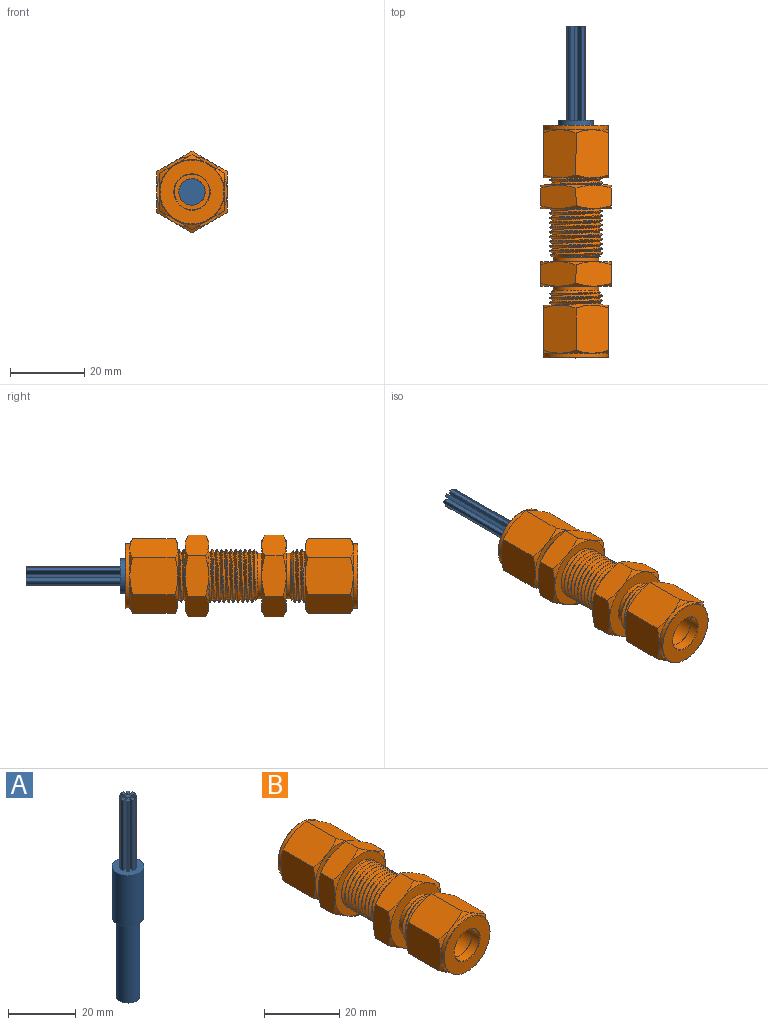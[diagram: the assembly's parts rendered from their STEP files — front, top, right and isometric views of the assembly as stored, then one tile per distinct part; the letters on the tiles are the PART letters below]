
ASSEMBLY  parts=2 mates=1
PART A: 38 faces, bbox 9.4x9.4x72.3 mm
  f0: plane 9.42x9.42mm, normal (0,0,1), area 57.7mm2, adj f3,f5,f6,f7,f8,f9,f10,f11
  f1: cylinder r=3.52mm len=28.65mm, axis (0,0,-1), area 633.3mm2, adj f2,f4
  f2: plane 7.04x7.04mm, normal (0,0,-1), area 38.9mm2, adj f1
  f3: cylinder r=4.71mm len=18.29mm, axis (0,0,-1), area 541.4mm2, adj f0,f4
  f4: plane 9.42x9.42mm, normal (0,0,-1), area 30.9mm2, adj f1,f3
  f5: plane 25.4x1.62mm, normal (-0.2,0.98,0), area 41.9mm2, adj f0,f6,f36,f37
  f6: cylinder r=0.95mm len=25.4mm, axis (0,0,-1), area 9.5mm2, adj f0,f5,f7,f37
  f7: plane 25.4x1.37mm, normal (0.56,-0.83,0), area 41.9mm2, adj f0,f6,f8,f37
  f8: cylinder r=2.6mm len=25.4mm, axis (0,0,-1), area 26mm2, adj f0,f7,f9,f37
  f9: plane 25.4x1.37mm, normal (-0.83,0.56,0), area 41.9mm2, adj f0,f8,f10,f37
  f10: cylinder r=0.95mm len=25.4mm, axis (0,0,-1), area 9.5mm2, adj f0,f9,f11,f37
  f11: plane 25.4x1.62mm, normal (0.98,-0.2,0), area 41.9mm2, adj f0,f10,f12,f37
  f12: cylinder r=2.6mm len=25.4mm, axis (0,0,-1), area 26mm2, adj f0,f11,f13,f37
  f13: plane 25.4x1.62mm, normal (-0.98,-0.2,0), area 41.9mm2, adj f0,f12,f14,f37
  f14: cylinder r=0.95mm len=25.4mm, axis (0,0,-1), area 9.5mm2, adj f0,f13,f15,f37
  f15: plane 25.4x1.37mm, normal (0.83,0.56,0), area 41.9mm2, adj f0,f14,f16,f37
  f16: cylinder r=2.6mm len=25.4mm, axis (0,0,-1), area 26mm2, adj f0,f15,f17,f37
  f17: plane 25.4x1.37mm, normal (-0.56,-0.83,0), area 41.9mm2, adj f0,f16,f18,f37
  f18: cylinder r=0.95mm len=25.4mm, axis (0,0,-1), area 9.5mm2, adj f0,f17,f19,f37
  f19: plane 25.4x1.62mm, normal (0.2,0.98,0), area 41.9mm2, adj f0,f18,f20,f37
  f20: cylinder r=2.6mm len=25.4mm, axis (0,0,-1), area 26mm2, adj f0,f19,f21,f37
  f21: plane 25.4x1.62mm, normal (0.2,-0.98,0), area 41.9mm2, adj f0,f20,f22,f37
  f22: cylinder r=0.95mm len=25.4mm, axis (0,0,-1), area 9.5mm2, adj f0,f21,f23,f37
  f23: plane 25.4x1.37mm, normal (-0.56,0.83,0), area 41.9mm2, adj f0,f22,f24,f37
  f24: cylinder r=2.6mm len=25.4mm, axis (0,0,-1), area 26mm2, adj f0,f23,f25,f37
  f25: plane 25.4x1.37mm, normal (0.83,-0.56,0), area 41.9mm2, adj f0,f24,f26,f37
  f26: cylinder r=0.95mm len=25.4mm, axis (0,0,-1), area 9.5mm2, adj f0,f25,f27,f37
  f27: plane 25.4x1.62mm, normal (-0.98,0.2,0), area 41.9mm2, adj f0,f26,f28,f37
  f28: cylinder r=2.6mm len=25.4mm, axis (0,0,-1), area 26mm2, adj f0,f27,f29,f37
  f29: plane 25.4x1.62mm, normal (0.98,0.2,0), area 41.9mm2, adj f0,f28,f30,f37
  f30: cylinder r=0.95mm len=25.4mm, axis (0,0,-1), area 9.5mm2, adj f0,f29,f31,f37
  f31: plane 25.4x1.37mm, normal (-0.83,-0.56,0), area 41.9mm2, adj f0,f30,f32,f37
  f32: cylinder r=2.6mm len=25.4mm, axis (0,0,-1), area 26mm2, adj f0,f31,f33,f37
  f33: plane 25.4x1.37mm, normal (0.56,0.83,0), area 41.9mm2, adj f0,f32,f34,f37
  f34: cylinder r=0.95mm len=25.4mm, axis (0,0,-1), area 9.5mm2, adj f0,f33,f35,f37
  f35: plane 25.4x1.62mm, normal (-0.2,-0.98,0), area 41.9mm2, adj f0,f34,f36,f37
  f36: cylinder r=2.6mm len=25.4mm, axis (0,0,-1), area 26mm2, adj f0,f5,f35,f37
  f37: plane 5.21x5.21mm, normal (0,0,1), area 12.1mm2, adj f5,f6,f7,f8,f9,f10,f11,f12
PART B: 148 faces, bbox 22.9x63.6x22.9 mm
  f0: plane 19.05x19.05mm, normal (0,1,0), area 124.7mm2, adj f2,f9,f10,f11,f12,f13,f14,f21
  f1: plane 19.05x19.05mm, normal (0,-1,0), area 124.7mm2, adj f2,f3,f4,f5,f6,f7,f8,f55
  f2: cylinder r=7.14mm len=14.29mm, axis (0,-1,0), area 249.4mm2, adj f0,f1,f72,f74
  f3: cone r=9.53mm half-angle=60deg, axis (0,1,0), area 8.9mm2, adj f1,f18,f19
  f4: cone r=9.53mm half-angle=60deg, axis (0,1,0), area 8.9mm2, adj f1,f17,f18
  f5: cone r=9.53mm half-angle=60deg, axis (0,1,0), area 8.9mm2, adj f1,f16,f17
  f6: cone r=9.53mm half-angle=60deg, axis (0,1,0), area 8.9mm2, adj f1,f15,f16
  f7: cone r=9.53mm half-angle=60deg, axis (0,1,0), area 8.9mm2, adj f1,f15,f20
  f8: cone r=9.53mm half-angle=60deg, axis (0,1,0), area 8.9mm2, adj f1,f19,f20
  f9: cone r=11mm half-angle=60deg, axis (0,-1,0), area 8.9mm2, adj f0,f18,f19
  f10: cone r=11mm half-angle=60deg, axis (0,-1,0), area 8.9mm2, adj f0,f17,f18
  f11: cone r=11mm half-angle=60deg, axis (0,-1,0), area 8.9mm2, adj f0,f16,f17
  f12: cone r=11mm half-angle=60deg, axis (0,-1,0), area 8.9mm2, adj f0,f15,f16
  f13: cone r=11mm half-angle=60deg, axis (0,-1,0), area 8.9mm2, adj f0,f15,f20
  f14: cone r=11mm half-angle=60deg, axis (0,-1,0), area 8.9mm2, adj f0,f19,f20
  f15: plane 10.43x7.26mm, normal (-0.5,0,0.87), area 63.4mm2, adj f6,f7,f12,f13,f16,f20
  f16: plane 11.91x7.26mm, normal (-1,0,0), area 63.4mm2, adj f5,f6,f11,f12,f15,f17
  f17: plane 10.43x7.26mm, normal (-0.5,0,-0.87), area 63.4mm2, adj f4,f5,f10,f11,f16,f18
  f18: plane 10.43x7.26mm, normal (0.5,0,-0.87), area 63.4mm2, adj f3,f4,f9,f10,f17,f19
  f19: plane 11.91x7.26mm, normal (1,0,0), area 63.4mm2, adj f3,f8,f9,f14,f18,f20
  f20: plane 10.43x7.26mm, normal (0.5,0,0.87), area 63.4mm2, adj f7,f8,f13,f14,f15,f19
  f21: cylinder r=7.14mm len=14.29mm, axis (0,1,0), area 10.7mm2, adj f0,f22,f72,f74
  f22: plane 17.46x17.46mm, normal (0,-1,0), area 79.2mm2, adj f21,f24,f25,f26,f27,f28,f29,f44
  f23: plane 17.21x17.21mm, normal (0,1,0), area 157.5mm2, adj f53,f54
  f24: cone r=10.08mm half-angle=60deg, axis (0,1,0), area 7.5mm2, adj f22,f31,f32
  f25: cone r=10.08mm half-angle=60deg, axis (0,1,0), area 7.5mm2, adj f22,f32,f33
  f26: cone r=10.08mm half-angle=60deg, axis (0,1,0), area 7.5mm2, adj f22,f33,f34
  f27: cone r=10.08mm half-angle=60deg, axis (0,1,0), area 7.5mm2, adj f22,f34,f35
  f28: cone r=10.08mm half-angle=60deg, axis (0,1,0), area 7.5mm2, adj f22,f30,f35
  f29: cone r=10.08mm half-angle=60deg, axis (0,1,0), area 7.5mm2, adj f22,f30,f31
  f30: plane 13.8x9.56mm, normal (0.5,0,-0.87), area 125.2mm2, adj f28,f29,f31,f35,f37,f42
  f31: plane 13.79x10.92mm, normal (1,0,0), area 125.2mm2, adj f24,f29,f30,f32,f41,f42
  f32: plane 13.8x9.56mm, normal (0.5,0,0.87), area 125.2mm2, adj f24,f25,f31,f33,f40,f41
  f33: plane 13.8x9.56mm, normal (-0.5,0,0.87), area 125.2mm2, adj f25,f26,f32,f34,f39,f40
  f34: plane 13.79x10.92mm, normal (-1,0,0), area 125.2mm2, adj f26,f27,f33,f35,f38,f39
  f35: plane 13.8x9.56mm, normal (-0.5,0,-0.87), area 125.2mm2, adj f27,f28,f30,f34,f37,f38
  f36: cylinder r=8.73mm len=17.46mm, axis (0,1,0), area 62.7mm2, adj f37,f38,f39,f40,f41,f42,f54
  f37: cone r=8.73mm half-angle=60deg, axis (0,-1,0), area 7.5mm2, adj f30,f35,f36
  f38: cone r=8.73mm half-angle=60deg, axis (0,-1,0), area 7.5mm2, adj f34,f35,f36
  f39: cone r=8.73mm half-angle=60deg, axis (0,-1,0), area 7.5mm2, adj f33,f34,f36
  f40: cone r=8.73mm half-angle=60deg, axis (0,-1,0), area 7.5mm2, adj f32,f33,f36
  f41: cone r=8.73mm half-angle=60deg, axis (0,-1,0), area 7.5mm2, adj f31,f32,f36
  f42: cone r=8.73mm half-angle=60deg, axis (0,-1,0), area 7.5mm2, adj f30,f31,f36
  f43: cylinder r=4.76mm len=9.53mm, axis (0,1,0), area 77.5mm2, adj f52,f53
  f44: cylinder r=7.14mm len=14.29mm, axis (0,1,0), area 14mm2, adj f22,f45,f72
  f45: cylinder r=7.14mm len=14.29mm, axis (0,1,0), area 49mm2, adj f22,f44,f46,f72,f74
  f46: cylinder r=7.14mm len=14.29mm, axis (0,1,0), area 49.9mm2, adj f45,f47,f72,f74
  f47: cylinder r=7.14mm len=14.29mm, axis (0,1,0), area 49.9mm2, adj f46,f48,f72,f74
  f48: cylinder r=7.14mm len=14.29mm, axis (0,1,0), area 187.6mm2, adj f47,f49,f72,f74,f109
  f49: plane 14.29x14.29mm, normal (0,-1,0), area 27.2mm2, adj f48,f50
  f50: cylinder r=6.51mm len=13.02mm, axis (0,1,0), area 116.3mm2, adj f49,f51
  f51: plane 13.02x13.02mm, normal (0,-1,0), area 11.4mm2, adj f50,f57
  f52: cone r=4.89mm half-angle=45deg, axis (0,-1,0), area 5.4mm2, adj f43,f56
  f53: cone r=4.76mm half-angle=45deg, axis (0,1,0), area 5.4mm2, adj f23,f43
  f54: cone r=8.6mm half-angle=45deg, axis (0,-1,0), area 9.8mm2, adj f23,f36
  f55: cylinder r=7.14mm len=14.29mm, axis (0,1,0), area 68.4mm2, adj f1,f72,f74,f111
  f56: plane 9.78x9.78mm, normal (0,1,0), area 3.9mm2, adj f52,f60
  f57: cylinder r=6.22mm len=12.45mm, axis (0,1,0), area 44.7mm2, adj f51,f58
  f58: plane 12.45x12.45mm, normal (0,-1,0), area 28.8mm2, adj f57,f59
  f59: cylinder r=5.44mm len=10.87mm, axis (0,1,0), area 26.5mm2, adj f58,f62
  f60: cylinder r=4.76mm len=9.53mm, axis (0,1,0), area 203.3mm2, adj f56,f63
  f61: cone r=5.08mm half-angle=13.9deg, axis (0,1,0), area 102.8mm2, adj f62,f75
  f62: plane 12.57x12.57mm, normal (0,1,0), area 31.3mm2, adj f59,f61
  f63: plane 10.16x10.16mm, normal (0,-1,0), area 9.8mm2, adj f60,f64
  f64: cone r=5.63mm half-angle=13.9deg, axis (0,1,0), area 40.9mm2, adj f63,f106
  f65: cylinder r=6.22mm len=12.45mm, axis (0,-1,0), area 44.7mm2, adj f66,f142
  f66: plane 12.45x12.45mm, normal (0,1,0), area 28.8mm2, adj f65,f67
  f67: cylinder r=5.44mm len=10.87mm, axis (0,-1,0), area 26.5mm2, adj f66,f69
  f68: cone r=5.08mm half-angle=13.9deg, axis (0,-1,0), area 102.8mm2, adj f69,f76
  f69: plane 12.57x12.57mm, normal (0,-1,0), area 31.3mm2, adj f67,f68
  f70: plane 10.16x10.16mm, normal (0,1,0), area 9.8mm2, adj f71,f146
  f71: cone r=4.76mm half-angle=13.9deg, axis (0,-1,0), area 40.9mm2, adj f70,f105
  f72: bspline ~30.3x14.27mm, area 869.4mm2, adj f2,f21,f44,f45,f46,f47,f48,f55
  f73: cylinder r=6.32mm len=27.96mm, axis (0,1,0), area 401.8mm2, adj f72,f74,f109,f110
  f74: bspline ~28.61x14.43mm, area 869.8mm2, adj f2,f21,f45,f46,f47,f48,f55,f73
  f75: plane 12.36x12.36mm, normal (0,1,0), area 20.6mm2, adj f61,f109
  f76: plane 12.36x12.36mm, normal (0,-1,0), area 20.6mm2, adj f68,f80
  f77: plane 19.05x19.05mm, normal (0,-1,0), area 165mm2, adj f79,f85,f86,f87,f88,f89,f90
  f78: cone r=7.28mm half-angle=45deg, axis (0,-1,0), area 31.9mm2, adj f79,f81,f82,f83,f84
  f79: cylinder r=6.18mm len=12.36mm, axis (0,-1,0), area 42.7mm2, adj f77,f78
  f80: cone r=6.18mm half-angle=45deg, axis (0,1,0), area 31.9mm2, adj f76,f81,f82,f83,f113
  f81: bspline ~14.43x14.43mm, area 306mm2, adj f78,f80,f82,f84,f113,f114,f115,f116
  f82: cylinder r=6.32mm len=12.64mm, axis (0,1,0), area 76.4mm2, adj f78,f80,f81,f83
  f83: bspline ~16.4x16.37mm, area 438.8mm2, adj f78,f80,f82,f84,f113,f115,f116,f117
  f84: cylinder r=7.14mm len=14.29mm, axis (0,1,0), area 16.9mm2, adj f78,f81,f83,f118
  f85: cone r=9.53mm half-angle=60deg, axis (0,1,0), area 8.9mm2, adj f77,f91,f92
  f86: cone r=9.53mm half-angle=60deg, axis (0,1,0), area 8.9mm2, adj f77,f92,f93
  f87: cone r=9.53mm half-angle=60deg, axis (0,1,0), area 8.9mm2, adj f77,f93,f94
  f88: cone r=9.53mm half-angle=60deg, axis (0,1,0), area 8.9mm2, adj f77,f94,f95
  f89: cone r=9.53mm half-angle=60deg, axis (0,1,0), area 8.9mm2, adj f77,f95,f96
  f90: cone r=9.53mm half-angle=60deg, axis (0,1,0), area 8.9mm2, adj f77,f91,f96
  f91: plane 11.91x7.52mm, normal (1,0,0), area 66.2mm2, adj f85,f90,f92,f96,f97,f102
  f92: plane 10.43x7.51mm, normal (0.5,0,-0.87), area 66.2mm2, adj f85,f86,f91,f93,f97,f98
  f93: plane 10.43x7.51mm, normal (-0.5,0,-0.87), area 66.2mm2, adj f86,f87,f92,f94,f98,f99
  f94: plane 11.91x7.52mm, normal (-1,0,0), area 66.2mm2, adj f87,f88,f93,f95,f99,f100
  f95: plane 10.43x7.51mm, normal (-0.5,0,0.87), area 66.2mm2, adj f88,f89,f94,f96,f100,f101
  f96: plane 10.43x7.51mm, normal (0.5,0,0.87), area 66.2mm2, adj f89,f90,f91,f95,f101,f102
  f97: cone r=11mm half-angle=60deg, axis (0,-1,0), area 8.9mm2, adj f91,f92,f103
  f98: cone r=11mm half-angle=60deg, axis (0,-1,0), area 8.9mm2, adj f92,f93,f103
  f99: cone r=11mm half-angle=60deg, axis (0,-1,0), area 8.9mm2, adj f93,f94,f103
  f100: cone r=11mm half-angle=60deg, axis (0,-1,0), area 8.9mm2, adj f94,f95,f103
  f101: cone r=11mm half-angle=60deg, axis (0,-1,0), area 8.9mm2, adj f95,f96,f103
  f102: cone r=11mm half-angle=60deg, axis (0,-1,0), area 8.9mm2, adj f91,f96,f103
  f103: plane 19.05x19.05mm, normal (0,1,0), area 165mm2, adj f97,f98,f99,f100,f101,f102,f112
  f104: plane 9.53x9.53mm, normal (0,-1,0), area 31.2mm2, adj f105,f108
  f105: cylinder r=4.76mm len=9.53mm, axis (0,-1,0), area 182.4mm2, adj f71,f104
  f106: cylinder r=4.76mm len=9.53mm, axis (0,-1,0), area 182.4mm2, adj f64,f107
  f107: plane 9.53x9.53mm, normal (0,1,0), area 31.2mm2, adj f106,f108
  f108: cylinder r=3.57mm len=28.64mm, axis (0,-1,0), area 642.2mm2, adj f104,f107
  f109: cone r=7.28mm half-angle=45deg, axis (0,-1,0), area 31.9mm2, adj f48,f72,f73,f74,f75
  f110: cone r=6.18mm half-angle=45deg, axis (0,1,0), area 29.9mm2, adj f72,f73,f74,f111,f112
  f111: cone r=6.18mm half-angle=45deg, axis (0,1,0), area 2.1mm2, adj f55,f72,f74,f110
  f112: cylinder r=6.18mm len=12.36mm, axis (0,-1,0), area 42.7mm2, adj f103,f110
  f113: cylinder r=7.14mm len=14.29mm, axis (0,-1,0), area 186.4mm2, adj f80,f81,f83,f117,f140
  f114: cylinder r=7.14mm len=14.29mm, axis (0,-1,0), area 15mm2, adj f81,f115,f118
  f115: cylinder r=7.14mm len=14.29mm, axis (0,-1,0), area 49.3mm2, adj f81,f83,f114,f116,f118
  f116: cylinder r=7.14mm len=14.29mm, axis (0,-1,0), area 49.9mm2, adj f81,f83,f115,f117
  f117: cylinder r=7.14mm len=14.29mm, axis (0,-1,0), area 49.9mm2, adj f81,f83,f113,f116
  f118: plane 17.46x17.46mm, normal (0,1,0), area 79.2mm2, adj f84,f114,f115,f120,f121,f122,f123,f124
  f119: plane 17.21x17.21mm, normal (0,-1,0), area 157.5mm2, adj f144,f145
  f120: cone r=10.08mm half-angle=60deg, axis (0,-1,0), area 7.5mm2, adj f118,f127,f128
  f121: cone r=10.08mm half-angle=60deg, axis (0,-1,0), area 7.5mm2, adj f118,f128,f129
  f122: cone r=10.08mm half-angle=60deg, axis (0,-1,0), area 7.5mm2, adj f118,f129,f130
  f123: cone r=10.08mm half-angle=60deg, axis (0,-1,0), area 7.5mm2, adj f118,f130,f131
  f124: cone r=10.08mm half-angle=60deg, axis (0,-1,0), area 7.5mm2, adj f118,f126,f131
  f125: cone r=10.08mm half-angle=60deg, axis (0,-1,0), area 7.5mm2, adj f118,f126,f127
  f126: plane 13.8x9.56mm, normal (0.5,0,0.87), area 125.2mm2, adj f124,f125,f127,f131,f133,f138
  f127: plane 13.79x10.92mm, normal (1,0,0), area 125.2mm2, adj f120,f125,f126,f128,f137,f138
  f128: plane 13.8x9.56mm, normal (0.5,0,-0.87), area 125.2mm2, adj f120,f121,f127,f129,f136,f137
  f129: plane 13.8x9.56mm, normal (-0.5,0,-0.87), area 125.2mm2, adj f121,f122,f128,f130,f135,f136
  f130: plane 13.79x10.92mm, normal (-1,0,0), area 125.2mm2, adj f122,f123,f129,f131,f134,f135
  f131: plane 13.8x9.56mm, normal (-0.5,0,0.87), area 125.2mm2, adj f123,f124,f126,f130,f133,f134
  f132: cylinder r=8.73mm len=17.46mm, axis (0,-1,0), area 62.7mm2, adj f133,f134,f135,f136,f137,f138,f145
  f133: cone r=8.73mm half-angle=60deg, axis (0,1,0), area 7.5mm2, adj f126,f131,f132
  f134: cone r=8.73mm half-angle=60deg, axis (0,1,0), area 7.5mm2, adj f130,f131,f132
  f135: cone r=8.73mm half-angle=60deg, axis (0,1,0), area 7.5mm2, adj f129,f130,f132
  f136: cone r=8.73mm half-angle=60deg, axis (0,1,0), area 7.5mm2, adj f128,f129,f132
  f137: cone r=8.73mm half-angle=60deg, axis (0,1,0), area 7.5mm2, adj f127,f128,f132
  f138: cone r=8.73mm half-angle=60deg, axis (0,1,0), area 7.5mm2, adj f126,f127,f132
  f139: cylinder r=4.76mm len=9.53mm, axis (0,-1,0), area 77.5mm2, adj f143,f144
  f140: plane 14.29x14.29mm, normal (0,1,0), area 27.2mm2, adj f113,f141
  f141: cylinder r=6.51mm len=13.02mm, axis (0,-1,0), area 116.3mm2, adj f140,f142
  f142: plane 13.02x13.02mm, normal (0,1,0), area 11.4mm2, adj f65,f141
  f143: cone r=4.89mm half-angle=45deg, axis (0,1,0), area 5.4mm2, adj f139,f147
  f144: cone r=4.76mm half-angle=45deg, axis (0,-1,0), area 5.4mm2, adj f119,f139
  f145: cone r=8.6mm half-angle=45deg, axis (0,1,0), area 9.8mm2, adj f119,f132
  f146: cylinder r=4.76mm len=9.53mm, axis (0,-1,0), area 203.3mm2, adj f70,f147
  f147: plane 9.78x9.78mm, normal (0,-1,0), area 3.9mm2, adj f143,f146
PLACE A rot(axis=(-1,0,0),90deg) t=(4.08,-3.55,12.63)mm
PLACE B t=(4.08,-20.56,12.63)mm
MATE fastened A.f3 <-> B.f64  axis (0,-1,0) through (4.08,25.1,12.63)mm
